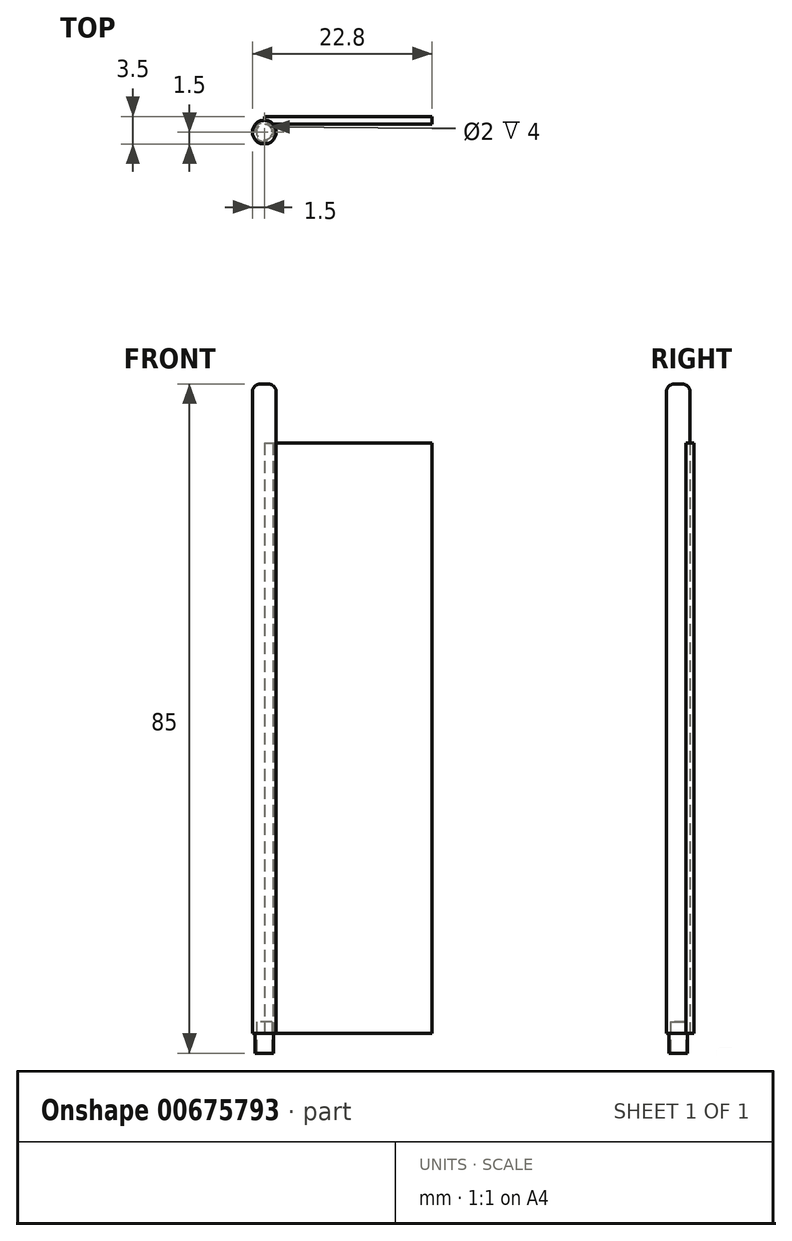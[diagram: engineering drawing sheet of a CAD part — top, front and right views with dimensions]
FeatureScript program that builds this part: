
annotation { "Feature Type Name" : "Feature", "Feature Type Description" : "" }
export const myFeature = defineFeature(function(context is Context, id is Id, definition is map)
    precondition{}
    {
        {
            var Q0;
            Q0=qCreatedBy(makeId("Top.planeOp"),FACE);
            var sketch = newSketch(context, id + "F0", { "sketchPlane" : qUnion([Q0])});
            skCircle(sketch, "E0", {"center": v(0, 0) * mm, "radius": 1.2 * mm});
            skCircle(sketch, "E1", {"center": v(0, 0) * mm, "radius": 1.5 * mm});
            skCircle(sketch, "E2", {"center": v(0, 0) * mm, "radius": 1 * mm});
            skSolve(sketch);
        }
        {
            var Q0;
            Q0=makeQuery(id+"F0.imprint","IMPRINT",FACE,{"disambiguationData":[TD([[makeQuery(id+"F0.imprint","IMPRINT",EDGE,{"derivedFrom":sQuery(id+"F0.wireOp",EDGE,"E2")}),1.0]])]});
            var Q1;
            Q1=makeQuery(id+"F0.imprint","IMPRINT",FACE,{"disambiguationData":[TD([[makeQuery(id+"F0.imprint","IMPRINT",EDGE,{"derivedFrom":sQuery(id+"F0.wireOp",EDGE,"E0")}),1.0]])]});
            var Q2;
            Q2=makeQuery(id+"F0.imprint","IMPRINT",FACE,{"disambiguationData":[TD([[makeQuery(id+"F0.imprint","IMPRINT",EDGE,{"derivedFrom":sQuery(id+"F0.wireOp",EDGE,"E0")}),-1.0]])]});
            extrude(context, id + "F1", {"entities" : qUnion([Q0, Q1, Q2]), "depth" : 85 * mm, "offsetDistance" : 25 * mm});
        }
        {
            var Q0;
            Q0=makeQuery(id+"F0.imprint","IMPRINT",FACE,{"disambiguationData":[TD([[makeQuery(id+"F0.imprint","IMPRINT",EDGE,{"derivedFrom":sQuery(id+"F0.wireOp",EDGE,"E0")}),-1.0]])]});
            extrude(context, id + "F2", {"entities" : qUnion([Q0]), "operationType" : NewBodyOperationType.REMOVE, "depth" : 2.5 * mm, "offsetDistance" : 25 * mm});
        }
        {
            var Q0;
            Q0=makeQuery(id+"F0.imprint","IMPRINT",FACE,{"disambiguationData":[TD([[makeQuery(id+"F0.imprint","IMPRINT",EDGE,{"derivedFrom":sQuery(id+"F0.wireOp",EDGE,"E2")}),1.0]])]});
            extrude(context, id + "F3", {"entities" : qUnion([Q0]), "operationType" : NewBodyOperationType.REMOVE, "depth" : 4 * mm, "offsetDistance" : 25 * mm});
        }
        {
            var Q0;
            Q0=makeQuery(id+"F1.opExtrude","CAP_EDGE",EDGE,{"disambiguationData":[OSD([sQuery(id+"F0.wireOp",EDGE,"E1")])],"isStart":false});
            fillet(context, id + "F4", {"entities" : qUnion([Q0]), "radius" : 1 * mm, "tangentPropagation" : true, "allowEdgeOverflow" : false});
        }
        {
            var Q0;
            Q0=qCreatedBy(makeId("Front.planeOp"),FACE);
            var sketch = newSketch(context, id + "F5", { "sketchPlane" : qUnion([Q0])});
            skLineSegment(sketch, "E3", {"start": v(0, 0) * mm, "end": v(0, 2.5) * mm});
            skLineSegment(sketch, "E4", {"start": v(0, 2.5) * mm, "end": v(0, 77.5) * mm});
            skLineSegment(sketch, "E5", {"start": v(0, 77.5) * mm, "end": v(21.3, 77.5) * mm});
            skLineSegment(sketch, "E6", {"start": v(21.3, 77.5) * mm, "end": v(21.3, 2.5) * mm});
            skLineSegment(sketch, "E7", {"start": v(0, 2.5) * mm, "end": v(21.3, 2.5) * mm});
            skSolve(sketch);
        }
        {
            var Q0;
            Q0=makeQuery(id+"F5.imprint","IMPRINT",FACE,{"disambiguationData":[TD([[makeQuery(id+"F5.imprint","IMPRINT",EDGE,{"derivedFrom":sQuery(id+"F5.wireOp",EDGE,"E4")}),-1.0]])]});
            extrude(context, id + "F6", {"entities" : qUnion([Q0]), "operationType" : NewBodyOperationType.ADD, "oppositeDirection" : true, "depth" : 2 * mm, "offsetDistance" : 25 * mm, "hasSecondDirection" : true, "secondDirectionOppositeDirection" : true, "secondDirectionDepth" : 1 * mm});
        }
    });
